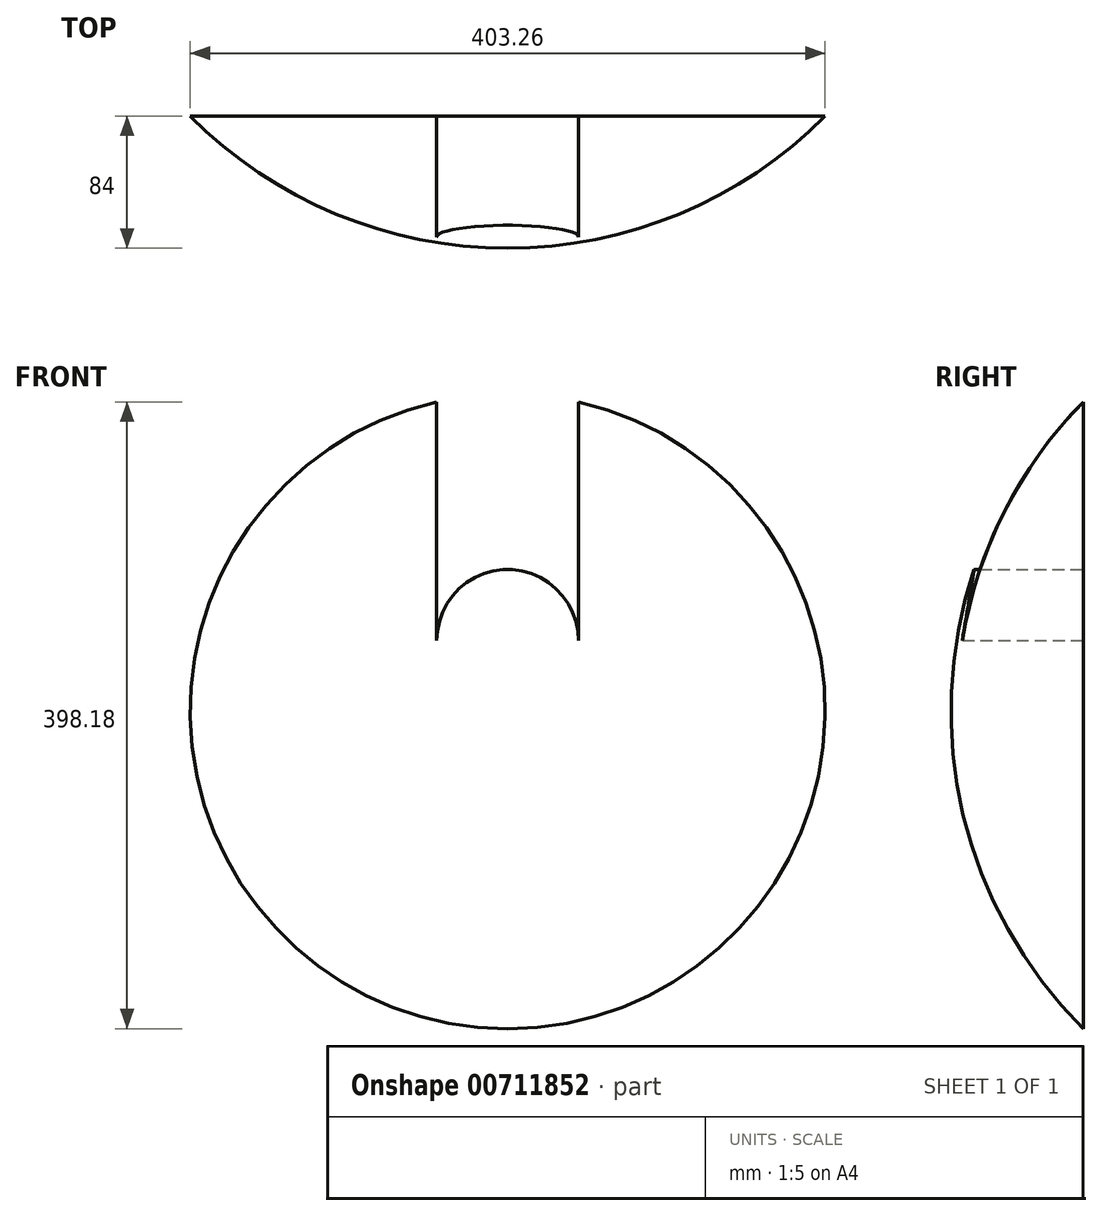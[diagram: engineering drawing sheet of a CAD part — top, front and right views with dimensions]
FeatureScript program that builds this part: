
annotation { "Feature Type Name" : "Feature", "Feature Type Description" : "" }
export const myFeature = defineFeature(function(context is Context, id is Id, definition is map)
    precondition{}
    {
        {
            var Q0;
            Q0=qCreatedBy(makeId("Front.planeOp"),FACE);
            var sketch = newSketch(context, id + "F0", { "sketchPlane" : qUnion([Q0])});
            skArc(sketch, "E0", {"start": v(284, 0) * mm, "mid": v(0, 284) * mm, "end": v(-284, 0) * mm});
            skPoint(sketch, "E1", {"position": v(-284, 0) * mm});
            skPoint(sketch, "E2", {"position": v(284, 0) * mm});
            skLineSegment(sketch, "E3", {"start": v(-284, 0) * mm, "end": v(284, 0) * mm});
            skSolve(sketch);
        }
        {
            var Q0;
            Q0=makeQuery(id+"F0.imprint","IMPRINT",FACE,{"disambiguationData":[TD([[makeQuery(id+"F0.imprint","IMPRINT",EDGE,{"derivedFrom":sQuery(id+"F0.wireOp",EDGE,"E0")}),1.0]])]});
            var Q1;
            Q1=sQuery(id+"F0.wireOp",EDGE,"E3");
            revolve(context, id + "F1", {"surfaceOperationType" : NewSurfaceOperationType.NEW, "entities" : qUnion([Q0]), "axis" : qUnion([Q1]), "revolveType" : RevolveType.FULL});
        }
        {
            var Q0;
            Q0=qCreatedBy(makeId("Front.planeOp"),FACE);
            cPlane(context, id + "F2", {"entities" : qUnion([Q0]), "cplaneType" : CPlaneType.OFFSET, "offset" : 200 * mm, "width" : 150 * mm, "height" : 150 * mm});
        }
        {
            var Q0;
            Q0=qCreatedBy(id+"F2.planeOp",FACE);
            var sketch = newSketch(context, id + "F3", { "sketchPlane" : qUnion([Q0])});
            skCircle(sketch, "E4", {"center": v(0, 0) * mm, "radius": 300 * mm});
            skSolve(sketch);
        }
        {
            var Q0;
            Q0=makeQuery(id+"F3.imprint","IMPRINT",FACE,{"disambiguationData":[TD([[makeQuery(id+"F3.imprint","IMPRINT",EDGE,{"derivedFrom":sQuery(id+"F3.wireOp",EDGE,"E4")}),1.0]])]});
            extrude(context, id + "F4", {"entities" : qUnion([Q0]), "operationType" : NewBodyOperationType.REMOVE, "oppositeDirection" : true, "depth" : 500 * mm, "offsetDistance" : 25 * mm});
        }
        {
            var Q0;
            Q0=qCreatedBy(makeId("Front.planeOp"),FACE);
            var sketch = newSketch(context, id + "F5", { "sketchPlane" : qUnion([Q0])});
            skCircle(sketch, "E5", {"center": v(0, 45) * mm, "radius": 45 * mm});
            skLineSegment(sketch, "E6.bottom", {"start": v(45, 45) * mm, "end": v(-45, 45) * mm});
            skLineSegment(sketch, "E6.top", {"start": v(45, 45) * mm, "end": v(-45, 45) * mm});
            skLineSegment(sketch, "E6.left", {"start": v(45, 45) * mm, "end": v(45, 45) * mm});
            skLineSegment(sketch, "E6.right", {"start": v(-45, 45) * mm, "end": v(-45, 45) * mm});
            skLineSegment(sketch, "E7.bottom", {"start": v(-45, 227.5) * mm, "end": v(45, 227.5) * mm});
            skLineSegment(sketch, "E7.top", {"start": v(-45, 45) * mm, "end": v(45, 45) * mm});
            skLineSegment(sketch, "E7.left", {"start": v(-45, 227.5) * mm, "end": v(-45, 45) * mm});
            skLineSegment(sketch, "E7.right", {"start": v(45, 227.5) * mm, "end": v(45, 45) * mm});
            skSolve(sketch);
        }
        {
            var Q0;
            Q0=makeQuery(id+"F5.imprint","IMPRINT",FACE,{"disambiguationData":[TD([[makeQuery(id+"F5.imprint","IMPRINT",EDGE,{"derivedFrom":sQuery(id+"F5.wireOp",EDGE,"E7.bottom")}),-1.0]])]});
            var Q1;
            {var subQ0=sQuery(id+"F5.wireOp",EDGE,"E7.top");Q1=makeQuery(id+"F5.imprint","IMPRINT",FACE,{"disambiguationData":[TD([[makeQuery(id+"F5.imprint","IMPRINT",EDGE,{"derivedFrom":subQ0}),1.0]])]});}
            var Q2;
            {var subQ0=sQuery(id+"F5.wireOp",EDGE,"E7.top");Q2=makeQuery(id+"F5.imprint","IMPRINT",FACE,{"disambiguationData":[TD([[makeQuery(id+"F5.imprint","IMPRINT",EDGE,{"derivedFrom":subQ0}),-1.0]])]});}
            extrude(context, id + "F6", {"entities" : qUnion([Q0, Q1, Q2]), "operationType" : NewBodyOperationType.REMOVE, "depth" : 600 * mm, "offsetDistance" : 25 * mm});
        }
    });
